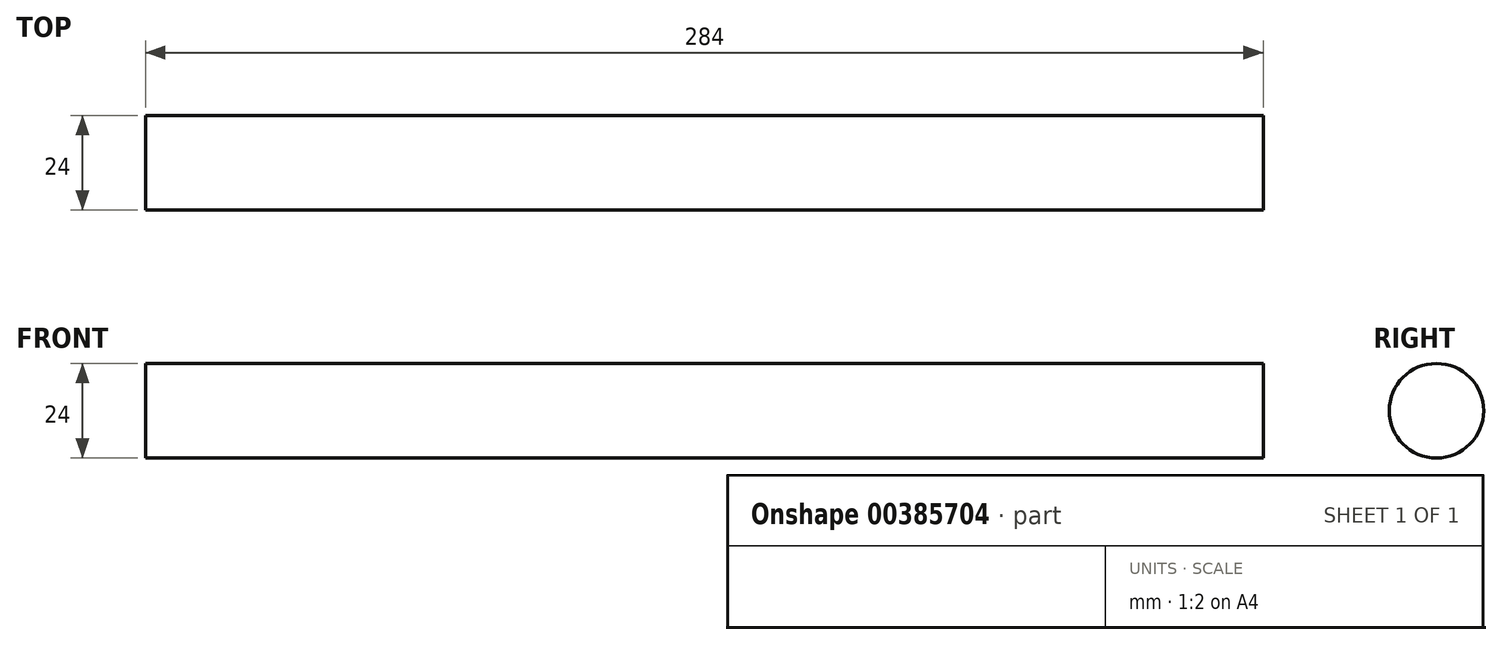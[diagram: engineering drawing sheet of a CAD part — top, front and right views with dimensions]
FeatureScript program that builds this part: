
annotation { "Feature Type Name" : "Feature", "Feature Type Description" : "" }
export const myFeature = defineFeature(function(context is Context, id is Id, definition is map)
    precondition{}
    {
        {
            var Q0;
            Q0=qCreatedBy(makeId("Right.planeOp"),FACE);
            var sketch = newSketch(context, id + "F0", { "sketchPlane" : qUnion([Q0])});
            skCircle(sketch, "E0", {"center": v(0, 0) * mm, "radius": 12 * mm});
            skSolve(sketch);
        }
        {
            var Q0;
            Q0=makeQuery(id+"F0.imprint","IMPRINT",FACE,{"disambiguationData":[TD([[makeQuery(id+"F0.imprint","IMPRINT",EDGE,{"derivedFrom":sQuery(id+"F0.wireOp",EDGE,"E0")}),1.0]])]});
            extrude(context, id + "F1", {"entities" : qUnion([Q0]), "endBound" : BoundingType.SYMMETRIC, "depth" : 284 * mm});
        }
    });
